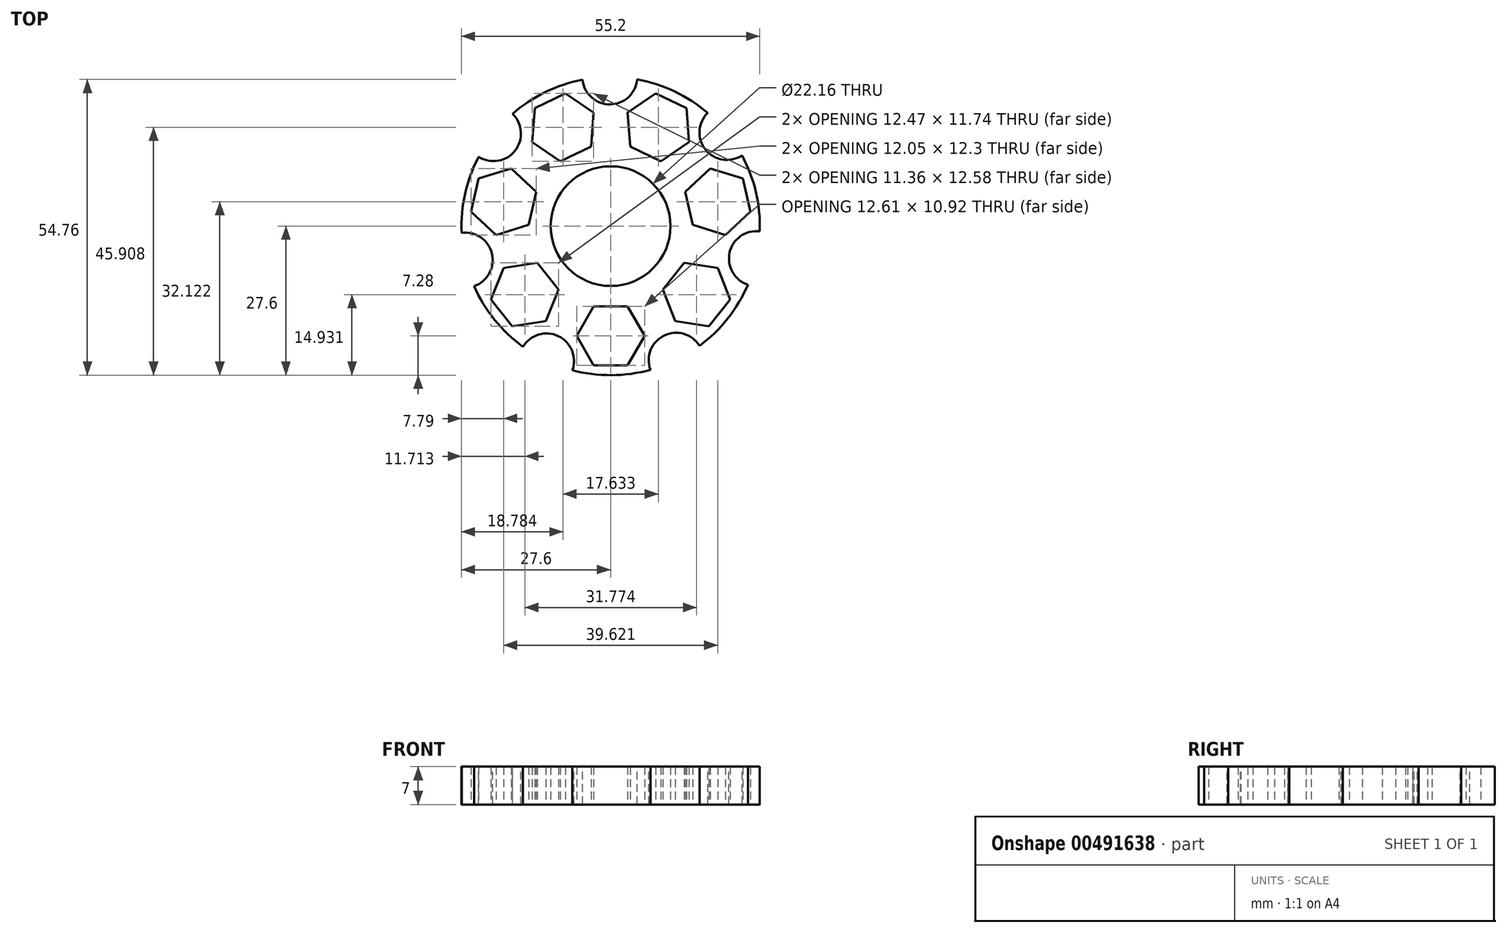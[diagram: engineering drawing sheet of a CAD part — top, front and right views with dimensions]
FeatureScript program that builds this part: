
annotation { "Feature Type Name" : "Feature", "Feature Type Description" : "" }
export const myFeature = defineFeature(function(context is Context, id is Id, definition is map)
    precondition{}
    {
        {
            var Q0;
            Q0=qCreatedBy(makeId("Top.planeOp"),FACE);
            var sketch = newSketch(context, id + "F0", { "sketchPlane" : qUnion([Q0])});
            skCircle(sketch, "E0", {"center": v(0, 0) * mm, "radius": 10.95 * mm});
            skCircle(sketch, "E1.cCircle", {"center": v(0, 0) * mm, "radius": 12.7 * mm, "construction": true});
            skPoint(sketch, "E2.endSnap0", {"position": v(0, -12.7) * mm});
            skPoint(sketch, "E3.0.midPoint", {"position": v(12.82, 7.4) * mm});
            skPoint(sketch, "E4.0.midPoint", {"position": v(12.82, -7.4) * mm});
            skPoint(sketch, "E5.0.midPoint", {"position": v(-12.82, -7.4) * mm});
            skPoint(sketch, "E6.0.midPoint", {"position": v(-12.87, 7.32) * mm});
            skPoint(sketch, "E7.0.midPoint", {"position": v(-10.5, 5.95) * mm});
            skPoint(sketch, "E8.0.midPoint", {"position": v(0.35, 12.06) * mm});
            skPoint(sketch, "E9.0.midPoint", {"position": v(10.45, 6.03) * mm});
            skPoint(sketch, "E10.0.midPoint", {"position": v(10.45, -6.03) * mm});
            skPoint(sketch, "E11.0.midPoint", {"position": v(0, -12.07) * mm});
            skPoint(sketch, "E12.0.midPoint", {"position": v(-10.45, -6.03) * mm});
            skLineSegment(sketch, "E13.bottom", {"start": v(-1.27, -12.7) * mm, "end": v(1.27, -12.7) * mm});
            skLineSegment(sketch, "E14.bottom", {"start": v(1.27, 12.7) * mm, "end": v(-1.27, 12.7) * mm});
            skLineSegment(sketch, "E15", {"start": v(10.3, 7.42) * mm, "end": v(11.63, 5.25) * mm});
            skLineSegment(sketch, "E16", {"start": v(11.58, -5.22) * mm, "end": v(10.36, -7.45) * mm});
            skLineSegment(sketch, "E17", {"start": v(-9.81, -7.13) * mm, "end": v(-11.08, -4.93) * mm});
            skLineSegment(sketch, "E18", {"start": v(-11.63, -5.25) * mm, "end": v(-11.08, -4.93) * mm});
            skLineSegment(sketch, "E19", {"start": v(-11.18, 6.04) * mm, "end": v(-9.86, 8.32) * mm});
            skLineSegment(sketch, "E20", {"start": v(-11.08, -4.93) * mm, "end": v(-9.81, -7.13) * mm});
            skLineSegment(sketch, "E21", {"start": v(-10.36, -7.45) * mm, "end": v(-9.81, -7.13) * mm});
            skLineSegment(sketch, "E22", {"start": v(-10.36, -7.45) * mm, "end": v(-11.63, -5.25) * mm});
            skCircle(sketch, "E23", {"center": v(0, 0) * mm, "radius": 11.08 * mm});
            skCircle(sketch, "E24", {"center": v(0, 0) * mm, "radius": 11.07 * mm});
            skLineSegment(sketch, "E25", {"start": v(0, 0) * mm, "end": v(0, -20.32) * mm});
            skLineSegment(sketch, "E26", {"start": v(0, 0) * mm, "end": v(-15.89, -12.67) * mm});
            skLineSegment(sketch, "E27", {"start": v(0, 0) * mm, "end": v(-19.81, 4.52) * mm});
            skLineSegment(sketch, "E28", {"start": v(0, 0) * mm, "end": v(-8.82, 18.3) * mm});
            skLineSegment(sketch, "E29", {"start": v(0, 0) * mm, "end": v(8.82, 18.3) * mm});
            skLineSegment(sketch, "E30", {"start": v(0, 0) * mm, "end": v(19.81, 4.52) * mm});
            skLineSegment(sketch, "E31", {"start": v(0, 0) * mm, "end": v(15.89, -12.67) * mm});
            skCircle(sketch, "E32.cCircle", {"center": v(0, -20.32) * mm, "radius": 6.99 * mm, "construction": true});
            skLineSegment(sketch, "E32.0", {"start": v(-4.03, -13.34) * mm, "end": v(4.03, -13.34) * mm});
            skLineSegment(sketch, "E32.1", {"start": v(4.03, -13.34) * mm, "end": v(8.07, -20.32) * mm});
            skLineSegment(sketch, "E32.2", {"start": v(8.07, -20.32) * mm, "end": v(4.03, -27.3) * mm});
            skLineSegment(sketch, "E32.3", {"start": v(4.03, -27.3) * mm, "end": v(-4.03, -27.3) * mm});
            skLineSegment(sketch, "E32.4", {"start": v(-4.03, -27.3) * mm, "end": v(-8.07, -20.32) * mm});
            skLineSegment(sketch, "E32.5", {"start": v(-8.07, -20.32) * mm, "end": v(-4.03, -13.33) * mm});
            skPoint(sketch, "E32.0.midPoint", {"position": v(0, -13.34) * mm});
            skCircle(sketch, "E33.cCircle", {"center": v(-15.89, -12.67) * mm, "radius": 6.98 * mm, "construction": true});
            skLineSegment(sketch, "E33.0", {"start": v(-12.94, -5.16) * mm, "end": v(-7.91, -11.47) * mm});
            skLineSegment(sketch, "E33.1", {"start": v(-7.91, -11.47) * mm, "end": v(-10.86, -18.98) * mm});
            skLineSegment(sketch, "E33.2", {"start": v(-10.86, -18.98) * mm, "end": v(-18.83, -20.18) * mm});
            skLineSegment(sketch, "E33.3", {"start": v(-18.83, -20.18) * mm, "end": v(-23.86, -13.87) * mm});
            skLineSegment(sketch, "E33.4", {"start": v(-23.86, -13.87) * mm, "end": v(-20.92, -6.36) * mm});
            skLineSegment(sketch, "E33.5", {"start": v(-20.92, -6.36) * mm, "end": v(-12.94, -5.16) * mm});
            skPoint(sketch, "E33.0.midPoint", {"position": v(-10.43, -8.31) * mm});
            skCircle(sketch, "E34.cCircle", {"center": v(-19.81, 4.52) * mm, "radius": 6.99 * mm, "construction": true});
            skLineSegment(sketch, "E34.0", {"start": v(-12.1, 6.9) * mm, "end": v(-13.9, -0.96) * mm});
            skLineSegment(sketch, "E34.1", {"start": v(-13.9, -0.96) * mm, "end": v(-21.6, -3.34) * mm});
            skLineSegment(sketch, "E34.2", {"start": v(-21.6, -3.34) * mm, "end": v(-27.52, 2.14) * mm});
            skLineSegment(sketch, "E34.3", {"start": v(-27.52, 2.14) * mm, "end": v(-25.72, 10) * mm});
            skLineSegment(sketch, "E34.4", {"start": v(-25.72, 10) * mm, "end": v(-18.02, 12.38) * mm});
            skLineSegment(sketch, "E34.5", {"start": v(-18.02, 12.38) * mm, "end": v(-12.1, 6.9) * mm});
            skPoint(sketch, "E34.0.midPoint", {"position": v(-13, 2.97) * mm});
            skCircle(sketch, "E35.cCircle", {"center": v(-8.82, 18.3) * mm, "radius": 6.99 * mm, "construction": true});
            skLineSegment(sketch, "E35.0", {"start": v(-2.15, 13.76) * mm, "end": v(-9.42, 10.26) * mm});
            skLineSegment(sketch, "E35.1", {"start": v(-9.42, 10.26) * mm, "end": v(-16.08, 14.8) * mm});
            skLineSegment(sketch, "E35.2", {"start": v(-16.08, 14.8) * mm, "end": v(-15.48, 22.85) * mm});
            skLineSegment(sketch, "E35.3", {"start": v(-15.48, 22.85) * mm, "end": v(-8.21, 26.35) * mm});
            skLineSegment(sketch, "E35.4", {"start": v(-8.21, 26.35) * mm, "end": v(-1.55, 21.8) * mm});
            skLineSegment(sketch, "E35.5", {"start": v(-1.55, 21.8) * mm, "end": v(-2.15, 13.76) * mm});
            skPoint(sketch, "E35.0.midPoint", {"position": v(-5.79, 12.01) * mm});
            skCircle(sketch, "E36.cCircle", {"center": v(8.82, 18.3) * mm, "radius": 6.99 * mm, "construction": true});
            skLineSegment(sketch, "E36.0", {"start": v(9.42, 10.26) * mm, "end": v(2.15, 13.76) * mm});
            skLineSegment(sketch, "E36.1", {"start": v(2.15, 13.76) * mm, "end": v(1.55, 21.8) * mm});
            skLineSegment(sketch, "E36.2", {"start": v(1.55, 21.8) * mm, "end": v(8.21, 26.35) * mm});
            skLineSegment(sketch, "E36.3", {"start": v(8.21, 26.35) * mm, "end": v(15.48, 22.85) * mm});
            skLineSegment(sketch, "E36.4", {"start": v(15.48, 22.85) * mm, "end": v(16.08, 14.8) * mm});
            skLineSegment(sketch, "E36.5", {"start": v(16.08, 14.8) * mm, "end": v(9.42, 10.26) * mm});
            skPoint(sketch, "E36.0.midPoint", {"position": v(5.79, 12.01) * mm});
            skCircle(sketch, "E37.cCircle", {"center": v(19.81, 4.52) * mm, "radius": 6.99 * mm, "construction": true});
            skLineSegment(sketch, "E37.0", {"start": v(13.9, -0.96) * mm, "end": v(12.1, 6.9) * mm});
            skLineSegment(sketch, "E37.1", {"start": v(12.1, 6.9) * mm, "end": v(18.02, 12.38) * mm});
            skLineSegment(sketch, "E37.2", {"start": v(18.02, 12.38) * mm, "end": v(25.72, 10) * mm});
            skLineSegment(sketch, "E37.3", {"start": v(25.72, 10) * mm, "end": v(27.52, 2.14) * mm});
            skLineSegment(sketch, "E37.4", {"start": v(27.52, 2.14) * mm, "end": v(21.6, -3.34) * mm});
            skLineSegment(sketch, "E37.5", {"start": v(21.6, -3.34) * mm, "end": v(13.9, -0.96) * mm});
            skPoint(sketch, "E37.0.midPoint", {"position": v(13, 2.97) * mm});
            skCircle(sketch, "E38.cCircle", {"center": v(15.89, -12.67) * mm, "radius": 6.99 * mm, "construction": true});
            skLineSegment(sketch, "E38.0", {"start": v(7.91, -11.47) * mm, "end": v(12.94, -5.16) * mm});
            skLineSegment(sketch, "E38.1", {"start": v(12.94, -5.16) * mm, "end": v(20.92, -6.36) * mm});
            skLineSegment(sketch, "E38.2", {"start": v(20.92, -6.36) * mm, "end": v(23.86, -13.87) * mm});
            skLineSegment(sketch, "E38.3", {"start": v(23.86, -13.87) * mm, "end": v(18.83, -20.18) * mm});
            skLineSegment(sketch, "E38.4", {"start": v(18.83, -20.18) * mm, "end": v(10.86, -18.98) * mm});
            skLineSegment(sketch, "E38.5", {"start": v(10.86, -18.98) * mm, "end": v(7.91, -11.47) * mm});
            skPoint(sketch, "E38.0.midPoint", {"position": v(10.43, -8.31) * mm});
            skCircle(sketch, "E39.cCircle", {"center": v(0, -20.32) * mm, "radius": 5.46 * mm, "construction": true});
            skLineSegment(sketch, "E39.0", {"start": v(-3.15, -14.86) * mm, "end": v(3.15, -14.86) * mm});
            skLineSegment(sketch, "E39.1", {"start": v(3.15, -14.86) * mm, "end": v(6.3, -20.32) * mm});
            skLineSegment(sketch, "E39.2", {"start": v(6.3, -20.32) * mm, "end": v(3.15, -25.78) * mm});
            skLineSegment(sketch, "E39.3", {"start": v(3.15, -25.78) * mm, "end": v(-3.15, -25.78) * mm});
            skLineSegment(sketch, "E39.4", {"start": v(-3.15, -25.78) * mm, "end": v(-6.3, -20.32) * mm});
            skLineSegment(sketch, "E39.5", {"start": v(-6.3, -20.32) * mm, "end": v(-3.15, -14.86) * mm});
            skPoint(sketch, "E39.0.midPoint", {"position": v(0, -14.86) * mm});
            skCircle(sketch, "E40.cCircle", {"center": v(-15.89, -12.67) * mm, "radius": 5.46 * mm, "construction": true});
            skLineSegment(sketch, "E40.0", {"start": v(-13.58, -6.8) * mm, "end": v(-9.65, -11.73) * mm});
            skLineSegment(sketch, "E40.1", {"start": v(-9.65, -11.73) * mm, "end": v(-11.96, -17.6) * mm});
            skLineSegment(sketch, "E40.2", {"start": v(-11.96, -17.6) * mm, "end": v(-18.2, -18.54) * mm});
            skLineSegment(sketch, "E40.3", {"start": v(-18.2, -18.54) * mm, "end": v(-22.12, -13.6) * mm});
            skLineSegment(sketch, "E40.4", {"start": v(-22.12, -13.6) * mm, "end": v(-19.82, -7.74) * mm});
            skLineSegment(sketch, "E40.5", {"start": v(-19.82, -7.74) * mm, "end": v(-13.58, -6.8) * mm});
            skPoint(sketch, "E40.0.midPoint", {"position": v(-11.62, -9.26) * mm});
            skPoint(sketch, "E41.0.midPoint", {"position": v(-15.89, 6.3) * mm});
            skCircle(sketch, "E42.cCircle", {"center": v(-8.82, 18.3) * mm, "radius": 5.46 * mm, "construction": true});
            skLineSegment(sketch, "E42.0", {"start": v(-3.6, 14.76) * mm, "end": v(-9.29, 12.02) * mm});
            skLineSegment(sketch, "E42.1", {"start": v(-9.29, 12.02) * mm, "end": v(-14.5, 15.57) * mm});
            skLineSegment(sketch, "E42.2", {"start": v(-14.5, 15.57) * mm, "end": v(-14.03, 21.86) * mm});
            skLineSegment(sketch, "E42.3", {"start": v(-14.03, 21.86) * mm, "end": v(-8.35, 24.6) * mm});
            skLineSegment(sketch, "E42.4", {"start": v(-8.35, 24.6) * mm, "end": v(-3.14, 21.04) * mm});
            skLineSegment(sketch, "E42.5", {"start": v(-3.14, 21.04) * mm, "end": v(-3.6, 14.76) * mm});
            skPoint(sketch, "E42.0.midPoint", {"position": v(-6.45, 13.39) * mm});
            skCircle(sketch, "E43.cCircle", {"center": v(8.82, 18.3) * mm, "radius": 5.46 * mm, "construction": true});
            skLineSegment(sketch, "E43.0", {"start": v(9.29, 12.02) * mm, "end": v(3.6, 14.76) * mm});
            skLineSegment(sketch, "E43.1", {"start": v(3.6, 14.76) * mm, "end": v(3.14, 21.04) * mm});
            skLineSegment(sketch, "E43.2", {"start": v(3.14, 21.04) * mm, "end": v(8.35, 24.6) * mm});
            skLineSegment(sketch, "E43.3", {"start": v(8.35, 24.6) * mm, "end": v(14.03, 21.86) * mm});
            skLineSegment(sketch, "E43.4", {"start": v(14.03, 21.86) * mm, "end": v(14.5, 15.57) * mm});
            skLineSegment(sketch, "E43.5", {"start": v(14.5, 15.57) * mm, "end": v(9.29, 12.02) * mm});
            skPoint(sketch, "E43.0.midPoint", {"position": v(6.45, 13.39) * mm});
            skPoint(sketch, "E44.0.midPoint", {"position": v(15.89, 7.7) * mm});
            skCircle(sketch, "E45.cCircle", {"center": v(15.89, -12.67) * mm, "radius": 5.46 * mm, "construction": true});
            skLineSegment(sketch, "E45.0", {"start": v(9.65, -11.73) * mm, "end": v(13.58, -6.8) * mm});
            skLineSegment(sketch, "E45.1", {"start": v(13.58, -6.8) * mm, "end": v(19.82, -7.74) * mm});
            skLineSegment(sketch, "E45.2", {"start": v(19.82, -7.74) * mm, "end": v(22.12, -13.6) * mm});
            skLineSegment(sketch, "E45.3", {"start": v(22.12, -13.6) * mm, "end": v(18.2, -18.54) * mm});
            skLineSegment(sketch, "E45.4", {"start": v(18.2, -18.54) * mm, "end": v(11.96, -17.6) * mm});
            skLineSegment(sketch, "E45.5", {"start": v(11.96, -17.6) * mm, "end": v(9.65, -11.73) * mm});
            skPoint(sketch, "E45.0.midPoint", {"position": v(11.62, -9.26) * mm});
            skCircle(sketch, "E46.cCircle", {"center": v(-19.81, 4.52) * mm, "radius": 5.46 * mm, "construction": true});
            skLineSegment(sketch, "E46.0", {"start": v(-13.78, 6.38) * mm, "end": v(-15.19, 0.23) * mm});
            skLineSegment(sketch, "E46.1", {"start": v(-15.19, 0.23) * mm, "end": v(-21.21, -1.63) * mm});
            skLineSegment(sketch, "E46.2", {"start": v(-21.21, -1.63) * mm, "end": v(-25.84, 2.66) * mm});
            skLineSegment(sketch, "E46.3", {"start": v(-25.84, 2.66) * mm, "end": v(-24.43, 8.81) * mm});
            skLineSegment(sketch, "E46.4", {"start": v(-24.43, 8.81) * mm, "end": v(-18.4, 10.67) * mm});
            skLineSegment(sketch, "E46.5", {"start": v(-18.4, 10.67) * mm, "end": v(-13.78, 6.38) * mm});
            skPoint(sketch, "E46.0.midPoint", {"position": v(-14.49, 3.3) * mm});
            skCircle(sketch, "E47.cCircle", {"center": v(19.81, 4.52) * mm, "radius": 5.46 * mm, "construction": true});
            skLineSegment(sketch, "E47.0", {"start": v(15.19, 0.23) * mm, "end": v(13.78, 6.38) * mm});
            skLineSegment(sketch, "E47.1", {"start": v(13.78, 6.38) * mm, "end": v(18.4, 10.67) * mm});
            skLineSegment(sketch, "E47.2", {"start": v(18.4, 10.67) * mm, "end": v(24.43, 8.81) * mm});
            skLineSegment(sketch, "E47.3", {"start": v(24.43, 8.81) * mm, "end": v(25.84, 2.66) * mm});
            skLineSegment(sketch, "E47.4", {"start": v(25.84, 2.66) * mm, "end": v(21.21, -1.63) * mm});
            skLineSegment(sketch, "E47.5", {"start": v(21.21, -1.63) * mm, "end": v(15.19, 0.23) * mm});
            skPoint(sketch, "E47.0.midPoint", {"position": v(14.49, 3.3) * mm});
            skPoint(sketch, "E48.midSnap0", {"position": v(4.73, -23.05) * mm});
            skPoint(sketch, "E48.midSnap1", {"position": v(6.05, -23.81) * mm});
            skCircle(sketch, "E49", {"center": v(0, 0) * mm, "radius": 27.6 * mm});
            skSolve(sketch);
        }
        {
            var Q0;
            Q0=qSketchRegion(id+"F0",true);
            var Q1;
            Q1=makeQuery(id+"F0.imprint","IMPRINT",FACE,{"disambiguationData":[TD([[makeQuery(id+"F0.imprint","IMPRINT",EDGE,{"derivedFrom":sQuery(id+"F0.wireOp",EDGE,"E14.bottom")}),-1.0]])]});
            var Q2;
            Q2=makeQuery(id+"F0.imprint","IMPRINT",FACE,{"disambiguationData":[TD([[makeQuery(id+"F0.imprint","IMPRINT",EDGE,{"derivedFrom":sQuery(id+"F0.wireOp",EDGE,"r9I69o4T-baSL-ddfZ-GocF-frNLYwVvmABk")}),1.0]])]});
            var Q3;
            Q3=makeQuery(id+"F0.imprint","IMPRINT",FACE,{"disambiguationData":[TD([[makeQuery(id+"F0.imprint","IMPRINT",EDGE,{"derivedFrom":sQuery(id+"F0.wireOp",EDGE,"E13.bottom")}),-1.0]])]});
            var Q4;
            {var subQ0=sQuery(id+"F0.wireOp",EDGE,"6sW6mJ2L-ygAF-Vdi4-I9HX-WlLPKnymDywZ");Q4=makeQuery(id+"F0.imprint","IMPRINT",FACE,{"disambiguationData":[TD([[makeQuery(id+"F0.imprint","IMPRINT",EDGE,{"derivedFrom":subQ0}),1.0]])]});}
            var Q5;
            {var subQ0=sQuery(id+"F0.wireOp",EDGE,"8BQQ6vlK-IiWs-5aLy-QiVH-YKUD170Bbk5W");Q5=makeQuery(id+"F0.imprint","IMPRINT",FACE,{"disambiguationData":[TD([[makeQuery(id+"F0.imprint","IMPRINT",EDGE,{"derivedFrom":subQ0}),1.0]])]});}
            var Q6;
            Q6=makeQuery(id+"F0.imprint","IMPRINT",FACE,{"disambiguationData":[TD([[makeQuery(id+"F0.imprint","IMPRINT",EDGE,{"derivedFrom":sQuery(id+"F0.wireOp",EDGE,"WzqIBDOR-9Q7D-lWyq-SiJA-YPrxWTZHhMYv")}),-1.0]])]});
            var Q7;
            {var subQ1=sQuery(id+"F0.wireOp",EDGE,"bpo8na64-lxTu-Gfvn-vT0u-1hGISmn388sy");Q7=makeQuery(id+"F0.imprint","IMPRINT",FACE,{"disambiguationData":[TD([[makeQuery(id+"F0.imprint","IMPRINT",EDGE,{"derivedFrom":subQ1}),-1.0]])]});}
            var Q8;
            {var subQ1=sQuery(id+"F0.wireOp",EDGE,"dw2wTLAi-85Je-w8Ac-Poy6-q1RHHzYaVD92");Q8=makeQuery(id+"F0.imprint","IMPRINT",FACE,{"disambiguationData":[TD([[makeQuery(id+"F0.imprint","IMPRINT",EDGE,{"derivedFrom":subQ1}),-1.0]])]});}
            var Q9;
            Q9=makeQuery(id+"F0.imprint","IMPRINT",FACE,{"disambiguationData":[TD([[makeQuery(id+"F0.imprint","IMPRINT",EDGE,{"derivedFrom":sQuery(id+"F0.wireOp",EDGE,"E18")}),-1.0]])]});
            extrude(context, id + "F1", {"entities" : qUnion([Q0, Q1, Q2, Q3, Q4, Q5, Q6, Q7, Q8, Q9]), "depth" : 7 * mm});
        }
        {
            var Q0;
            Q0=makeQuery(id+"F2.boolean.opBoolean","MERGE",FACE,{"derivedFrom":[makeQuery(id+"F1.opExtrude","CAP_FACE",FACE,{"disambiguationData":[OSD([sQuery(id+"F0.wireOp",EDGE,"E0"),sQuery(id+"F0.wireOp",EDGE,"E18"),sQuery(id+"F0.wireOp",EDGE,"E20"),sQuery(id+"F0.wireOp",EDGE,"E21"),sQuery(id+"F0.wireOp",EDGE,"E22"),sQuery(id+"F0.wireOp",EDGE,"E39.0"),sQuery(id+"F0.wireOp",EDGE,"E39.1"),sQuery(id+"F0.wireOp",EDGE,"E39.2"),sQuery(id+"F0.wireOp",EDGE,"E39.3"),sQuery(id+"F0.wireOp",EDGE,"E39.4"),sQuery(id+"F0.wireOp",EDGE,"E39.5"),sQuery(id+"F0.wireOp",EDGE,"E40.0"),sQuery(id+"F0.wireOp",EDGE,"E40.1"),sQuery(id+"F0.wireOp",EDGE,"E40.2"),sQuery(id+"F0.wireOp",EDGE,"E40.3"),sQuery(id+"F0.wireOp",EDGE,"E40.4"),sQuery(id+"F0.wireOp",EDGE,"E40.5"),sQuery(id+"F0.wireOp",EDGE,"E42.0"),sQuery(id+"F0.wireOp",EDGE,"E42.1"),sQuery(id+"F0.wireOp",EDGE,"E42.2"),sQuery(id+"F0.wireOp",EDGE,"E42.3"),sQuery(id+"F0.wireOp",EDGE,"E42.4"),sQuery(id+"F0.wireOp",EDGE,"E42.5"),sQuery(id+"F0.wireOp",EDGE,"E43.0"),sQuery(id+"F0.wireOp",EDGE,"E43.1"),sQuery(id+"F0.wireOp",EDGE,"E43.2"),sQuery(id+"F0.wireOp",EDGE,"E43.3"),sQuery(id+"F0.wireOp",EDGE,"E43.4"),sQuery(id+"F0.wireOp",EDGE,"E43.5"),sQuery(id+"F0.wireOp",EDGE,"E45.0"),sQuery(id+"F0.wireOp",EDGE,"E45.1"),sQuery(id+"F0.wireOp",EDGE,"E45.2"),sQuery(id+"F0.wireOp",EDGE,"E45.3"),sQuery(id+"F0.wireOp",EDGE,"E45.4"),sQuery(id+"F0.wireOp",EDGE,"E45.5"),sQuery(id+"F0.wireOp",EDGE,"E46.0"),sQuery(id+"F0.wireOp",EDGE,"E46.1"),sQuery(id+"F0.wireOp",EDGE,"E46.2"),sQuery(id+"F0.wireOp",EDGE,"E46.3"),sQuery(id+"F0.wireOp",EDGE,"E46.4"),sQuery(id+"F0.wireOp",EDGE,"E46.5"),sQuery(id+"F0.wireOp",EDGE,"E47.0"),sQuery(id+"F0.wireOp",EDGE,"E47.1"),sQuery(id+"F0.wireOp",EDGE,"E47.2"),sQuery(id+"F0.wireOp",EDGE,"E47.3"),sQuery(id+"F0.wireOp",EDGE,"E47.4"),sQuery(id+"F0.wireOp",EDGE,"E47.5"),sQuery(id+"F0.wireOp",EDGE,"E49")])],"isStart":false}),makeQuery(id+"F2.opExtrude","CAP_FACE",FACE,{"disambiguationData":[OSD([sQuery(id+"FYjbckoFbouVvZr_1.wireOp",EDGE,"KEPwEQ8B-iRMg-ZX9D-gUsf-C824259YZIXu"),sQuery(id+"FYjbckoFbouVvZr_1.wireOp",EDGE,"fee08b2a-0dad-45f9-b1e3-1ce1950c639a.0"),sQuery(id+"FYjbckoFbouVvZr_1.wireOp",EDGE,"fee08b2a-0dad-45f9-b1e3-1ce1950c639a.1"),sQuery(id+"FYjbckoFbouVvZr_1.wireOp",EDGE,"fee08b2a-0dad-45f9-b1e3-1ce1950c639a.2"),sQuery(id+"FYjbckoFbouVvZr_1.wireOp",EDGE,"fee08b2a-0dad-45f9-b1e3-1ce1950c639a.3"),sQuery(id+"FYjbckoFbouVvZr_1.wireOp",EDGE,"fee08b2a-0dad-45f9-b1e3-1ce1950c639a.4"),sQuery(id+"FYjbckoFbouVvZr_1.wireOp",EDGE,"fee08b2a-0dad-45f9-b1e3-1ce1950c639a.5")])],"isStart":false})]});
            var sketch = newSketch(context, id + "F3", { "sketchPlane" : qUnion([Q0])});
            skCircle(sketch, "E50.cCircle", {"center": v(0, 0) * mm, "radius": 24.9 * mm, "construction": true});
            skLineSegment(sketch, "E50.0", {"start": v(-21.69, 17.12) * mm, "end": v(-0.14, 27.63) * mm});
            skLineSegment(sketch, "E50.1", {"start": v(-0.14, 27.63) * mm, "end": v(21.51, 17.34) * mm});
            skLineSegment(sketch, "E50.2", {"start": v(21.51, 17.34) * mm, "end": v(26.97, -6.01) * mm});
            skLineSegment(sketch, "E50.3", {"start": v(26.97, -6.01) * mm, "end": v(12.11, -24.83) * mm});
            skLineSegment(sketch, "E50.4", {"start": v(12.11, -24.83) * mm, "end": v(-11.86, -24.95) * mm});
            skLineSegment(sketch, "E50.5", {"start": v(-11.86, -24.95) * mm, "end": v(-26.9, -6.28) * mm});
            skLineSegment(sketch, "E50.6", {"start": v(-26.9, -6.28) * mm, "end": v(-21.69, 17.12) * mm});
            skPoint(sketch, "E50.0.midPoint", {"position": v(-10.91, 22.37) * mm});
            skSolve(sketch);
        }
        {
            var Q0;
            Q0=sQuery(id+"F3.wireOp",VERTEX,"E50.6.end");
            var Q1;
            Q1=sQuery(id+"F3.wireOp",VERTEX,"E50.1.start");
            var Q2;
            Q2=sQuery(id+"F3.wireOp",VERTEX,"E50.2.start");
            var Q3;
            Q3=sQuery(id+"F3.wireOp",VERTEX,"E50.3.start");
            var Q4;
            Q4=sQuery(id+"F3.wireOp",VERTEX,"E50.4.start");
            var Q5;
            Q5=sQuery(id+"F3.wireOp",VERTEX,"E50.5.start");
            var Q6;
            Q6=sQuery(id+"F3.wireOp",VERTEX,"E50.6.start");
            var Q7;
            Q7=makeQuery(id+"F1.opExtrude","SWEPT_BODY",BODY,{"disambiguationData":[OSD([sQuery(id+"F0.wireOp",EDGE,"E0"),sQuery(id+"F0.wireOp",EDGE,"E18"),sQuery(id+"F0.wireOp",EDGE,"E20"),sQuery(id+"F0.wireOp",EDGE,"E21"),sQuery(id+"F0.wireOp",EDGE,"E22"),sQuery(id+"F0.wireOp",EDGE,"E39.0"),sQuery(id+"F0.wireOp",EDGE,"E39.1"),sQuery(id+"F0.wireOp",EDGE,"E39.2"),sQuery(id+"F0.wireOp",EDGE,"E39.3"),sQuery(id+"F0.wireOp",EDGE,"E39.4"),sQuery(id+"F0.wireOp",EDGE,"E39.5"),sQuery(id+"F0.wireOp",EDGE,"E40.0"),sQuery(id+"F0.wireOp",EDGE,"E40.1"),sQuery(id+"F0.wireOp",EDGE,"E40.2"),sQuery(id+"F0.wireOp",EDGE,"E40.3"),sQuery(id+"F0.wireOp",EDGE,"E40.4"),sQuery(id+"F0.wireOp",EDGE,"E40.5"),sQuery(id+"F0.wireOp",EDGE,"E42.0"),sQuery(id+"F0.wireOp",EDGE,"E42.1"),sQuery(id+"F0.wireOp",EDGE,"E42.2"),sQuery(id+"F0.wireOp",EDGE,"E42.3"),sQuery(id+"F0.wireOp",EDGE,"E42.4"),sQuery(id+"F0.wireOp",EDGE,"E42.5"),sQuery(id+"F0.wireOp",EDGE,"E43.0"),sQuery(id+"F0.wireOp",EDGE,"E43.1"),sQuery(id+"F0.wireOp",EDGE,"E43.2"),sQuery(id+"F0.wireOp",EDGE,"E43.3"),sQuery(id+"F0.wireOp",EDGE,"E43.4"),sQuery(id+"F0.wireOp",EDGE,"E43.5"),sQuery(id+"F0.wireOp",EDGE,"E45.0"),sQuery(id+"F0.wireOp",EDGE,"E45.1"),sQuery(id+"F0.wireOp",EDGE,"E45.2"),sQuery(id+"F0.wireOp",EDGE,"E45.3"),sQuery(id+"F0.wireOp",EDGE,"E45.4"),sQuery(id+"F0.wireOp",EDGE,"E45.5"),sQuery(id+"F0.wireOp",EDGE,"E46.0"),sQuery(id+"F0.wireOp",EDGE,"E46.1"),sQuery(id+"F0.wireOp",EDGE,"E46.2"),sQuery(id+"F0.wireOp",EDGE,"E46.3"),sQuery(id+"F0.wireOp",EDGE,"E46.4"),sQuery(id+"F0.wireOp",EDGE,"E46.5"),sQuery(id+"F0.wireOp",EDGE,"E47.0"),sQuery(id+"F0.wireOp",EDGE,"E47.1"),sQuery(id+"F0.wireOp",EDGE,"E47.2"),sQuery(id+"F0.wireOp",EDGE,"E47.3"),sQuery(id+"F0.wireOp",EDGE,"E47.4"),sQuery(id+"F0.wireOp",EDGE,"E47.5"),sQuery(id+"F0.wireOp",EDGE,"E49")])]});
            hole(context, id + "F4", {"style" : HoleStyle.SIMPLE, "endStyle" : HoleEndStyle.THROUGH, "holeDiameter" : 10.16 * mm, "majorDiameter" : 6.35 * mm, "isTappedThrough" : true, "tappedDepth" : 12.7 * mm, "tapClearance" : 3, "locations" : qUnion([Q0, Q1, Q2, Q3, Q4, Q5, Q6]), "scope" : qUnion([Q7])});
        }
    });
